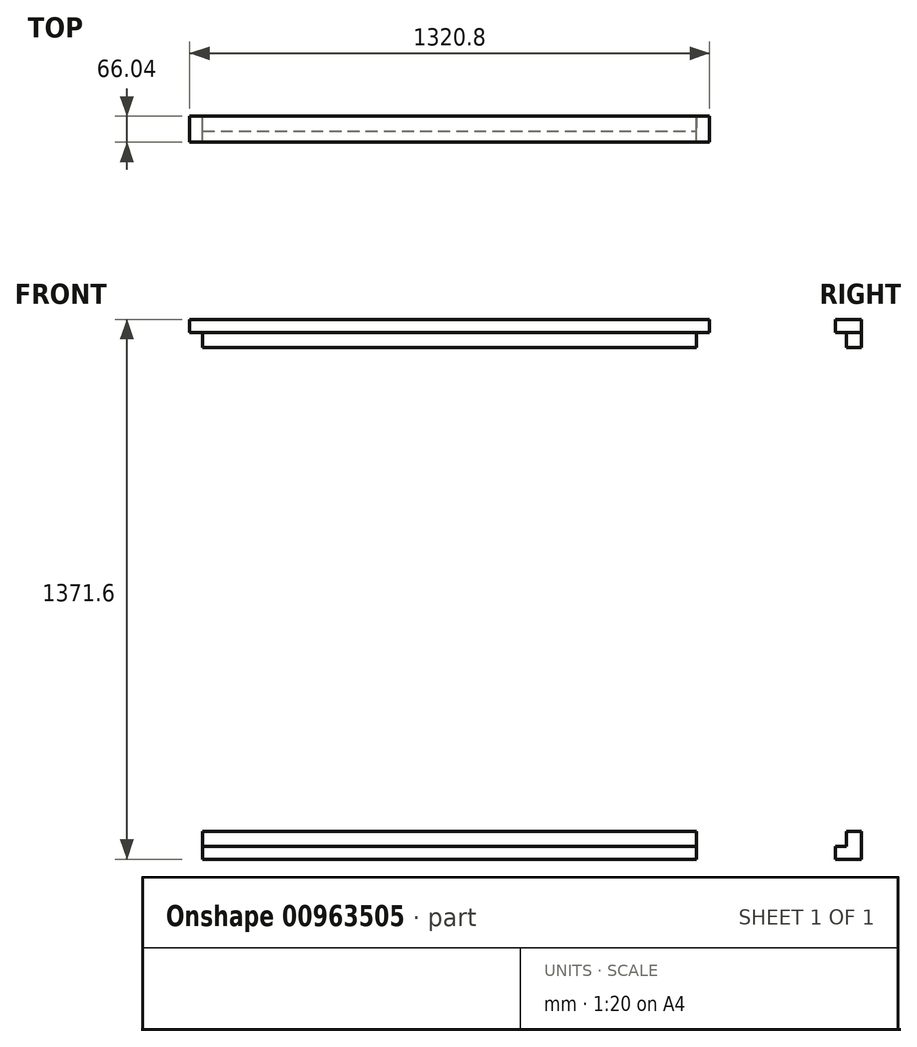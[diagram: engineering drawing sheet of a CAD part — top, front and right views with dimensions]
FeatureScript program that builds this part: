
annotation { "Feature Type Name" : "Feature", "Feature Type Description" : "" }
export const myFeature = defineFeature(function(context is Context, id is Id, definition is map)
    precondition{}
    {
        {
            var Q0;
            Q0=qCreatedBy(makeId("Front.planeOp"),FACE);
            var sketch = newSketch(context, id + "F0", { "sketchPlane" : qUnion([Q0])});
            skLineSegment(sketch, "E0.bottom", {"start": v(0, 0) * mm, "end": v(1320.8, 0) * mm});
            skLineSegment(sketch, "E0.top", {"start": v(0, -33.02) * mm, "end": v(1320.8, -33.02) * mm});
            skLineSegment(sketch, "E0.left", {"start": v(0, 0) * mm, "end": v(0, -33.02) * mm});
            skLineSegment(sketch, "E0.right", {"start": v(1320.8, 0) * mm, "end": v(1320.8, -33.02) * mm});
            skLineSegment(sketch, "E1.bottom", {"start": v(0, -33.02) * mm, "end": v(33.02, -33.02) * mm});
            skLineSegment(sketch, "E1.top", {"start": v(0, -1403.35) * mm, "end": v(33.02, -1403.35) * mm});
            skLineSegment(sketch, "E1.left", {"start": v(0, -33.02) * mm, "end": v(0, -1403.35) * mm});
            skLineSegment(sketch, "E1.right", {"start": v(33.02, -33.02) * mm, "end": v(33.02, -1403.35) * mm});
            skLineSegment(sketch, "E2.bottom", {"start": v(1320.8, -33.02) * mm, "end": v(1287.78, -33.02) * mm});
            skLineSegment(sketch, "E2.top", {"start": v(1320.8, -1403.35) * mm, "end": v(1287.78, -1403.35) * mm});
            skLineSegment(sketch, "E2.left", {"start": v(1320.8, -33.02) * mm, "end": v(1320.8, -1403.35) * mm});
            skLineSegment(sketch, "E2.right", {"start": v(1287.78, -33.02) * mm, "end": v(1287.78, -1403.35) * mm});
            skLineSegment(sketch, "E3.bottom", {"start": v(33.02, -1338.58) * mm, "end": v(1287.78, -1338.58) * mm});
            skLineSegment(sketch, "E3.top", {"start": v(33.02, -1371.6) * mm, "end": v(1287.78, -1371.6) * mm});
            skLineSegment(sketch, "E3.left", {"start": v(33.02, -1338.58) * mm, "end": v(33.02, -1371.6) * mm});
            skLineSegment(sketch, "E3.right", {"start": v(1287.78, -1338.58) * mm, "end": v(1287.78, -1371.6) * mm});
            skSolve(sketch);
        }
        {
            var Q0;
            Q0=qCreatedBy(makeId("Front.planeOp"),FACE);
            var sketch = newSketch(context, id + "F1", { "sketchPlane" : qUnion([Q0])});
            skLineSegment(sketch, "E4.bottom", {"start": v(33.02, -33.02) * mm, "end": v(1287.78, -33.02) * mm});
            skLineSegment(sketch, "E4.top", {"start": v(33.02, -71.12) * mm, "end": v(1287.78, -71.12) * mm});
            skLineSegment(sketch, "E4.left", {"start": v(33.02, -33.02) * mm, "end": v(33.02, -71.12) * mm});
            skLineSegment(sketch, "E4.right", {"start": v(1287.78, -33.02) * mm, "end": v(1287.78, -71.12) * mm});
            skLineSegment(sketch, "E5.bottom", {"start": v(33.02, -1338.58) * mm, "end": v(1287.78, -1338.58) * mm});
            skLineSegment(sketch, "E5.top", {"start": v(33.02, -1300.48) * mm, "end": v(1287.78, -1300.48) * mm});
            skLineSegment(sketch, "E5.left", {"start": v(33.02, -1338.58) * mm, "end": v(33.02, -1300.48) * mm});
            skLineSegment(sketch, "E5.right", {"start": v(1287.78, -1338.58) * mm, "end": v(1287.78, -1300.48) * mm});
            skLineSegment(sketch, "E6.bottom", {"start": v(1287.78, -1300.48) * mm, "end": v(1249.68, -1300.48) * mm});
            skLineSegment(sketch, "E6.top", {"start": v(1287.78, -71.12) * mm, "end": v(1249.68, -71.12) * mm});
            skLineSegment(sketch, "E6.left", {"start": v(1287.78, -1300.48) * mm, "end": v(1287.78, -71.12) * mm});
            skLineSegment(sketch, "E6.right", {"start": v(1249.68, -1300.48) * mm, "end": v(1249.68, -71.12) * mm});
            skLineSegment(sketch, "E7.bottom", {"start": v(33.02, -71.12) * mm, "end": v(71.12, -71.12) * mm});
            skLineSegment(sketch, "E7.top", {"start": v(33.02, -1300.48) * mm, "end": v(71.12, -1300.48) * mm});
            skLineSegment(sketch, "E7.left", {"start": v(33.02, -71.12) * mm, "end": v(33.02, -1300.48) * mm});
            skLineSegment(sketch, "E7.right", {"start": v(71.12, -71.12) * mm, "end": v(71.12, -1300.48) * mm});
            skSolve(sketch);
        }
        {
            var Q0;
            Q0=makeQuery(id+"F0.imprint","IMPRINT",FACE,{"disambiguationData":[TD([[makeQuery(id+"F0.imprint","IMPRINT",EDGE,{"derivedFrom":sQuery(id+"F0.wireOp",EDGE,"E3.bottom")}),-1.0]])]});
            var Q1;
            {var subQ1=sQuery(id+"F0.wireOp",EDGE,"E1.bottom");Q1=makeQuery(id+"F0.imprint","IMPRINT",FACE,{"disambiguationData":[TD([[makeQuery(id+"F0.imprint","IMPRINT",EDGE,{"derivedFrom":subQ1}),-1.0]])]});}
            var Q2;
            Q2=makeQuery(id+"F0.imprint","IMPRINT",FACE,{"disambiguationData":[TD([[makeQuery(id+"F0.imprint","IMPRINT",EDGE,{"derivedFrom":sQuery(id+"F0.wireOp",EDGE,"E0.bottom")}),-1.0]])]});
            var Q3;
            {var subQ1=sQuery(id+"F0.wireOp",EDGE,"E2.bottom");Q3=makeQuery(id+"F0.imprint","IMPRINT",FACE,{"disambiguationData":[TD([[makeQuery(id+"F0.imprint","IMPRINT",EDGE,{"derivedFrom":subQ1}),1.0]])]});}
            extrude(context, id + "F2", {"entities" : qUnion([Q0, Q1, Q2, Q3]), "depth" : 66.04 * mm, "offsetDistance" : 25.4 * mm});
        }
        {
            var Q0;
            Q0=makeQuery(id+"F1.imprint","IMPRINT",FACE,{"disambiguationData":[TD([[makeQuery(id+"F1.imprint","IMPRINT",EDGE,{"derivedFrom":sQuery(id+"F1.wireOp",EDGE,"E7.bottom")}),-1.0]])]});
            var Q1;
            Q1=makeQuery(id+"F1.imprint","IMPRINT",FACE,{"disambiguationData":[TD([[makeQuery(id+"F1.imprint","IMPRINT",EDGE,{"derivedFrom":sQuery(id+"F1.wireOp",EDGE,"E4.bottom")}),-1.0]])]});
            var Q2;
            Q2=makeQuery(id+"F1.imprint","IMPRINT",FACE,{"disambiguationData":[TD([[makeQuery(id+"F1.imprint","IMPRINT",EDGE,{"derivedFrom":sQuery(id+"F1.wireOp",EDGE,"E6.bottom")}),-1.0]])]});
            var Q3;
            Q3=makeQuery(id+"F1.imprint","IMPRINT",FACE,{"disambiguationData":[TD([[makeQuery(id+"F1.imprint","IMPRINT",EDGE,{"derivedFrom":sQuery(id+"F1.wireOp",EDGE,"E5.bottom")}),1.0]])]});
            extrude(context, id + "F3", {"entities" : qUnion([Q0, Q1, Q2, Q3]), "operationType" : NewBodyOperationType.ADD, "depth" : 38.1 * mm, "offsetDistance" : 25.4 * mm});
        }
    });
